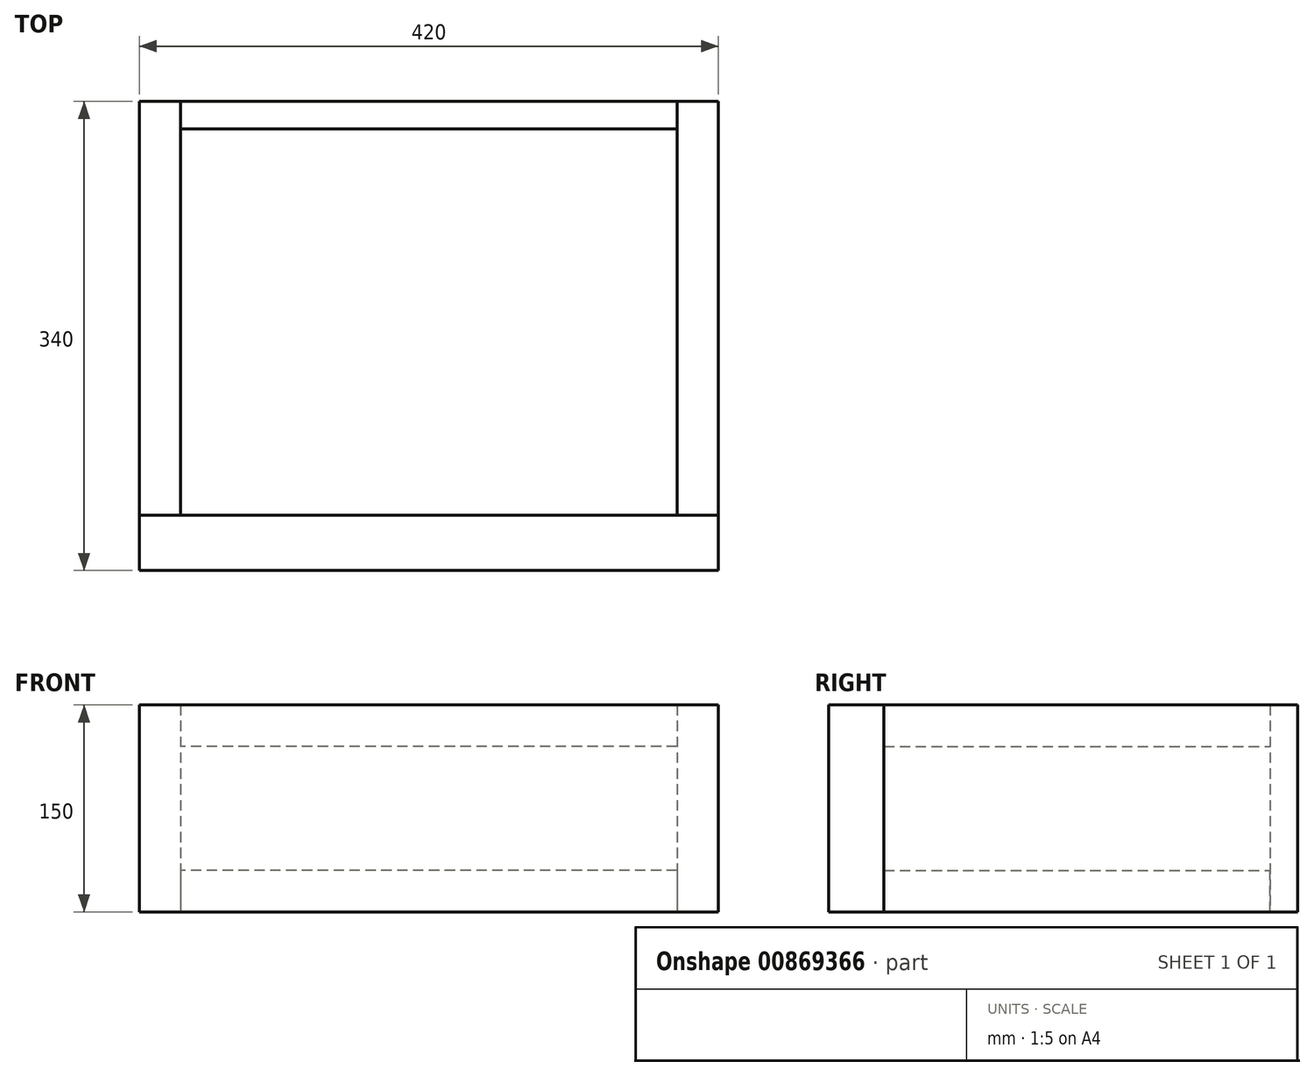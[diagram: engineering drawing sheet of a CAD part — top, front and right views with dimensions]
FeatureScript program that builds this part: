
annotation { "Feature Type Name" : "Feature", "Feature Type Description" : "" }
export const myFeature = defineFeature(function(context is Context, id is Id, definition is map)
    precondition{}
    {
        {
            var Q0;
            Q0=qCreatedBy(makeId("Right.planeOp"),FACE);
            var sketch = newSketch(context, id + "F0", { "sketchPlane" : qUnion([Q0])});
            skLineSegment(sketch, "E0.bottom", {"start": v(0, 0) * mm, "end": v(40, 0) * mm});
            skLineSegment(sketch, "E0.top", {"start": v(0, -150) * mm, "end": v(40, -150) * mm});
            skLineSegment(sketch, "E0.left", {"start": v(0, 0) * mm, "end": v(0, -150) * mm});
            skLineSegment(sketch, "E0.right", {"start": v(40, 0) * mm, "end": v(40, -150) * mm});
            skLineSegment(sketch, "E1.bottom", {"start": v(40, 0) * mm, "end": v(320, 0) * mm});
            skLineSegment(sketch, "E1.top", {"start": v(40, -30) * mm, "end": v(320, -30) * mm});
            skLineSegment(sketch, "E1.left", {"start": v(40, 0) * mm, "end": v(40, -30) * mm});
            skLineSegment(sketch, "E1.right", {"start": v(320, 0) * mm, "end": v(320, -30) * mm});
            skLineSegment(sketch, "E2.bottom", {"start": v(40, -150) * mm, "end": v(320, -150) * mm});
            skLineSegment(sketch, "E2.top", {"start": v(40, -120) * mm, "end": v(320, -120) * mm});
            skLineSegment(sketch, "E2.left", {"start": v(40, -150) * mm, "end": v(40, -120) * mm});
            skLineSegment(sketch, "E2.right", {"start": v(320, -150) * mm, "end": v(320, -120) * mm});
            skLineSegment(sketch, "E3.bottom", {"start": v(320, 0) * mm, "end": v(340, 0) * mm});
            skLineSegment(sketch, "E3.top", {"start": v(320, -150) * mm, "end": v(340, -150) * mm});
            skLineSegment(sketch, "E3.left", {"start": v(320, 0) * mm, "end": v(320, -150) * mm});
            skLineSegment(sketch, "E3.right", {"start": v(340, 0) * mm, "end": v(340, -150) * mm});
            skSolve(sketch);
        }
        {
            var Q0;
            Q0=makeQuery(id+"F0.imprint","IMPRINT",FACE,{"disambiguationData":[TD([[makeQuery(id+"F0.imprint","IMPRINT",EDGE,{"derivedFrom":sQuery(id+"F0.wireOp",EDGE,"E0.bottom")}),-1.0]])]});
            extrude(context, id + "F1", {"entities" : qUnion([Q0]), "endBound" : BoundingType.SYMMETRIC, "depth" : 420 * mm, "offsetDistance" : 25 * mm});
        }
        {
            var Q0;
            Q0=makeQuery(id+"F0.imprint","IMPRINT",FACE,{"disambiguationData":[TD([[makeQuery(id+"F0.imprint","IMPRINT",EDGE,{"derivedFrom":sQuery(id+"F0.wireOp",EDGE,"E1.bottom")}),-1.0]])]});
            extrude(context, id + "F2", {"entities" : qUnion([Q0]), "endBound" : BoundingType.SYMMETRIC, "depth" : 360 * mm, "offsetDistance" : 25 * mm});
        }
        {
            var Q0;
            Q0=makeQuery(id+"F0.imprint","IMPRINT",FACE,{"disambiguationData":[TD([[makeQuery(id+"F0.imprint","IMPRINT",EDGE,{"derivedFrom":sQuery(id+"F0.wireOp",EDGE,"E2.bottom")}),1.0]])]});
            extrude(context, id + "F3", {"entities" : qUnion([Q0]), "endBound" : BoundingType.SYMMETRIC, "depth" : 360 * mm, "offsetDistance" : 25 * mm});
        }
        {
            var Q0;
            Q0=makeQuery(id+"F1.opExtrude","SWEPT_FACE",FACE,{"disambiguationData":[OSD([sQuery(id+"F0.wireOp",EDGE,"E0.right"),sQuery(id+"F0.wireOp",EDGE,"E1.left"),sQuery(id+"F0.wireOp",EDGE,"E2.left")])]});
            var sketch = newSketch(context, id + "F4", { "sketchPlane" : qUnion([Q0])});
            skPoint(sketch, "E4.0", {"position": v(-180, 0) * mm});
            skPoint(sketch, "E4.1", {"position": v(180, 0) * mm});
            skLineSegment(sketch, "E5.bottom", {"start": v(-180, 0) * mm, "end": v(-210, 0) * mm});
            skLineSegment(sketch, "E5.top", {"start": v(-180, -150) * mm, "end": v(-210, -150) * mm});
            skLineSegment(sketch, "E5.left", {"start": v(-180, 0) * mm, "end": v(-180, -150) * mm});
            skLineSegment(sketch, "E5.right", {"start": v(-210, 0) * mm, "end": v(-210, -150) * mm});
            skLineSegment(sketch, "E6.bottom", {"start": v(180, 0) * mm, "end": v(210, 0) * mm});
            skLineSegment(sketch, "E6.top", {"start": v(180, -150) * mm, "end": v(210, -150) * mm});
            skLineSegment(sketch, "E6.left", {"start": v(180, 0) * mm, "end": v(180, -150) * mm});
            skLineSegment(sketch, "E6.right", {"start": v(210, 0) * mm, "end": v(210, -150) * mm});
            skSolve(sketch);
        }
        {
            var Q0;
            Q0=makeQuery(id+"F4.imprint","IMPRINT",FACE,{"disambiguationData":[TD([[makeQuery(id+"F4.imprint","IMPRINT",EDGE,{"derivedFrom":sQuery(id+"F4.wireOp",EDGE,"E5.bottom")}),-1.0]])]});
            extrude(context, id + "F5", {"entities" : qUnion([Q0]), "depth" : 300 * mm, "offsetDistance" : 25 * mm});
        }
        {
            var Q0;
            Q0=makeQuery(id+"F4.imprint","IMPRINT",FACE,{"disambiguationData":[TD([[makeQuery(id+"F4.imprint","IMPRINT",EDGE,{"derivedFrom":sQuery(id+"F4.wireOp",EDGE,"E6.bottom")}),-1.0]])]});
            extrude(context, id + "F6", {"entities" : qUnion([Q0]), "depth" : 300 * mm, "offsetDistance" : 25 * mm});
        }
        {
            var Q0;
            {var subQ3=sQuery(id+"F0.wireOp",EDGE,"E3.bottom");Q0=makeQuery(id+"F0.imprint","IMPRINT",FACE,{"disambiguationData":[TD([[makeQuery(id+"F0.imprint","IMPRINT",EDGE,{"derivedFrom":subQ3}),-1.0]])]});}
            extrude(context, id + "F7", {"entities" : qUnion([Q0]), "endBound" : BoundingType.SYMMETRIC, "depth" : 360 * mm, "offsetDistance" : 25 * mm});
        }
    });
